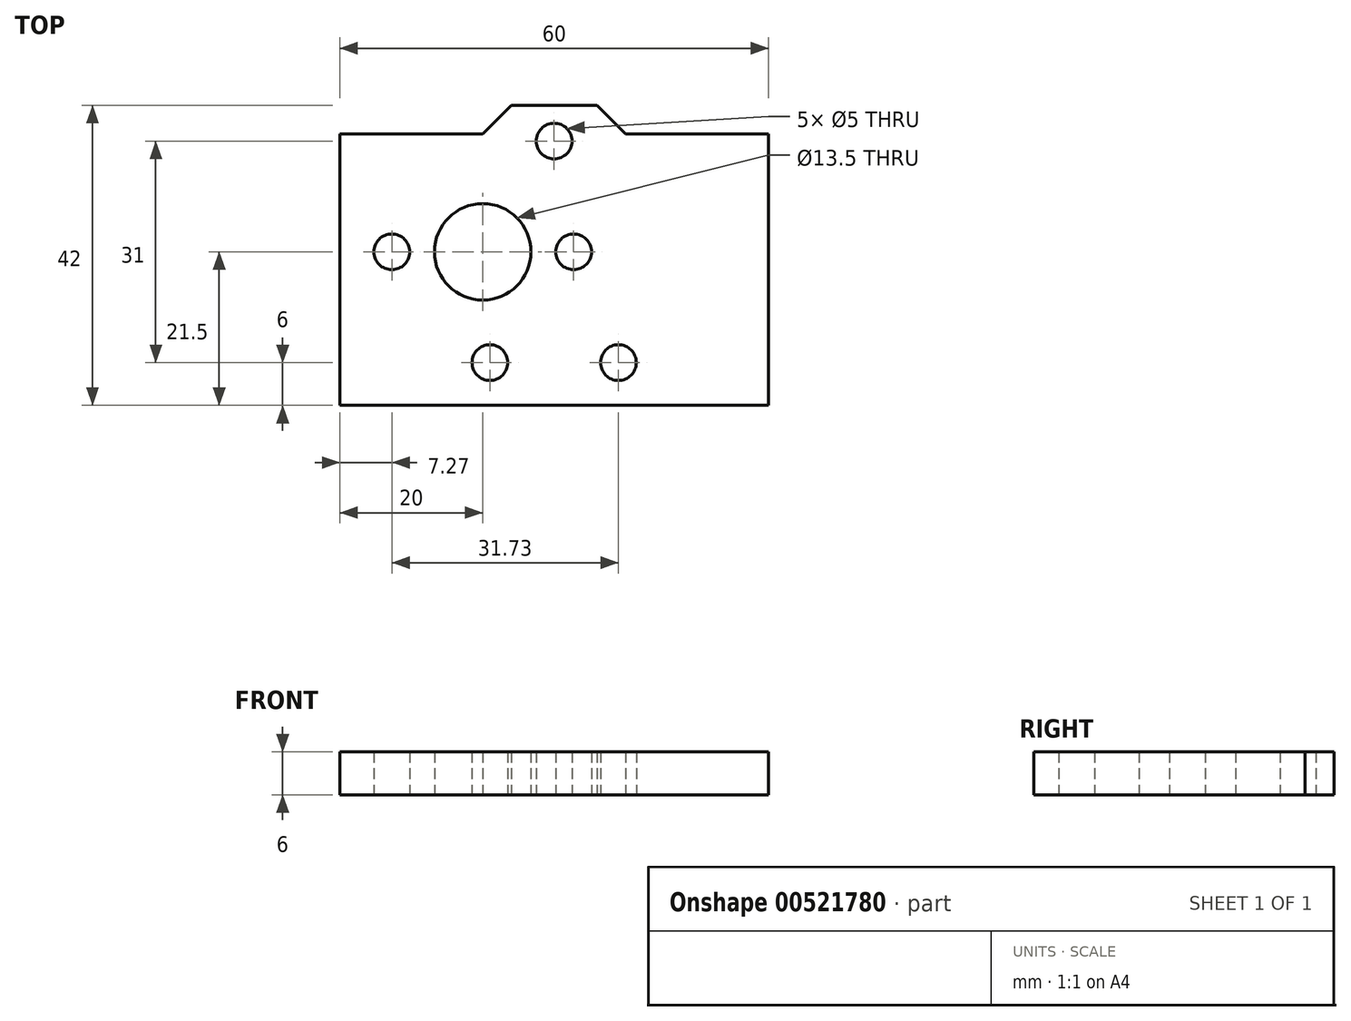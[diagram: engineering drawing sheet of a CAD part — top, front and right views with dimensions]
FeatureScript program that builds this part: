
annotation { "Feature Type Name" : "Feature", "Feature Type Description" : "" }
export const myFeature = defineFeature(function(context is Context, id is Id, definition is map)
    precondition{}
    {
        {
            var Q0;
            Q0=qCreatedBy(makeId("Top.planeOp"),FACE);
            var sketch = newSketch(context, id + "F0", { "sketchPlane" : qUnion([Q0])});
            skLineSegment(sketch, "E0.bottom", {"start": v(20, 10.5) * mm, "end": v(-20, 10.5) * mm});
            skLineSegment(sketch, "E0.top", {"start": v(20, -10.5) * mm, "end": v(-20, -10.5) * mm});
            skLineSegment(sketch, "E0.left", {"start": v(20, 10.5) * mm, "end": v(20, -10.5) * mm});
            skLineSegment(sketch, "E0.right", {"start": v(-20, 10.5) * mm, "end": v(-20, -10.5) * mm});
            skPoint(sketch, "E0.middle", {"position": v(0, 0) * mm});
            skLineSegment(sketch, "E1.0", {"start": v(20, 16.5) * mm, "end": v(10, 16.5) * mm});
            skLineSegment(sketch, "E2.0", {"start": v(20, -22.5) * mm, "end": v(-20, -22.5) * mm});
            skLineSegment(sketch, "E3.0", {"start": v(-30, 10.5) * mm, "end": v(-30, -10.5) * mm});
            skLineSegment(sketch, "E4.0", {"start": v(30, 10.5) * mm, "end": v(30, -10.5) * mm});
            skLineSegment(sketch, "E5", {"start": v(-20, 16.5) * mm, "end": v(-30, 16.5) * mm});
            skLineSegment(sketch, "E6", {"start": v(-30, 16.5) * mm, "end": v(-30, 10.5) * mm});
            skLineSegment(sketch, "E7", {"start": v(-30, -10.5) * mm, "end": v(-30, -22.5) * mm});
            skLineSegment(sketch, "E8", {"start": v(-30, -22.5) * mm, "end": v(-20, -22.5) * mm});
            skLineSegment(sketch, "E9", {"start": v(20, -22.5) * mm, "end": v(30, -22.5) * mm});
            skLineSegment(sketch, "E10", {"start": v(30, -22.5) * mm, "end": v(30, -10.5) * mm});
            skLineSegment(sketch, "E11", {"start": v(30, 10.5) * mm, "end": v(30, 16.5) * mm});
            skLineSegment(sketch, "E12", {"start": v(30, 16.5) * mm, "end": v(20, 16.5) * mm});
            skPoint(sketch, "E13", {"position": v(0, -10.5) * mm});
            skPoint(sketch, "E14", {"position": v(-9, -10.5) * mm});
            skPoint(sketch, "E15", {"position": v(9, -10.5) * mm});
            skPoint(sketch, "E16", {"position": v(-9, -15.5) * mm});
            skPoint(sketch, "E17", {"position": v(9, -15.5) * mm});
            skCircle(sketch, "E18", {"center": v(-9, -15.5) * mm, "radius": 2.5 * mm});
            skCircle(sketch, "E19", {"center": v(9, -15.5) * mm, "radius": 2.5 * mm});
            skPoint(sketch, "E20", {"position": v(-20, 0) * mm});
            skPoint(sketch, "E21", {"position": v(20, 0) * mm});
            skPoint(sketch, "E22", {"position": v(-10, 0) * mm});
            skCircle(sketch, "E23", {"center": v(-10, 0) * mm, "radius": 6.75 * mm});
            skPoint(sketch, "E24", {"position": v(-22.73, 0) * mm});
            skPoint(sketch, "E25", {"position": v(2.73, 0) * mm});
            skCircle(sketch, "E26", {"center": v(-22.73, 0) * mm, "radius": 2.5 * mm});
            skCircle(sketch, "E27", {"center": v(2.73, 0) * mm, "radius": 2.5 * mm});
            skPoint(sketch, "E28", {"position": v(0, 16.5) * mm});
            skLineSegment(sketch, "E29.bottom", {"start": v(6, 20.5) * mm, "end": v(-6, 20.5) * mm});
            skPoint(sketch, "E30", {"position": v(0, 15.5) * mm});
            skPoint(sketch, "E31", {"position": v(-10, 16.5) * mm});
            skPoint(sketch, "E32", {"position": v(10, 16.5) * mm});
            skLineSegment(sketch, "E33", {"start": v(-10, 16.5) * mm, "end": v(-6, 20.5) * mm});
            skLineSegment(sketch, "E34", {"start": v(6, 20.5) * mm, "end": v(10, 16.5) * mm});
            skCircle(sketch, "E35", {"center": v(0, 15.5) * mm, "radius": 2.5 * mm});
            skPoint(sketch, "E36", {"position": v(-2.3, 16.5) * mm});
            skPoint(sketch, "E37", {"position": v(2.3, 16.5) * mm});
            skLineSegment(sketch, "E38.trimOffspring", {"start": v(-10, 16.5) * mm, "end": v(-20, 16.5) * mm});
            skPoint(sketch, "E29.top.end.orphan", {"position": v(-6, 12.5) * mm});
            skPoint(sketch, "E29.top.start.orphan", {"position": v(6, 12.5) * mm});
            skSolve(sketch);
        }
        {
            var Q0;
            Q0=makeQuery(id+"F0.imprint","IMPRINT",FACE,{"disambiguationData":[TD([[makeQuery(id+"F0.imprint","IMPRINT",EDGE,{"derivedFrom":sQuery(id+"F0.wireOp",EDGE,"E0.bottom")}),-1.0]])]});
            var Q1;
            Q1=makeQuery(id+"F0.imprint","IMPRINT",FACE,{"disambiguationData":[TD([[makeQuery(id+"F0.imprint","IMPRINT",EDGE,{"derivedFrom":sQuery(id+"F0.wireOp",EDGE,"E0.bottom")}),1.0]])]});
            extrude(context, id + "F1", {"entities" : qUnion([Q0, Q1]), "depth" : 6 * mm, "offsetDistance" : 25 * mm});
        }
        {
            var Q0;
            Q0=makeQuery(id+"F1.opExtrude","SWEPT_FACE",FACE,{"disambiguationData":[OSD([sQuery(id+"F0.wireOp",EDGE,"E2.0"),sQuery(id+"F0.wireOp",EDGE,"E8"),sQuery(id+"F0.wireOp",EDGE,"E9")])]});
            extrude(context, id + "F2", {"entities" : qUnion([Q0]), "operationType" : NewBodyOperationType.REMOVE, "oppositeDirection" : true, "depth" : 1 * mm, "offsetDistance" : 25 * mm});
        }
    });
